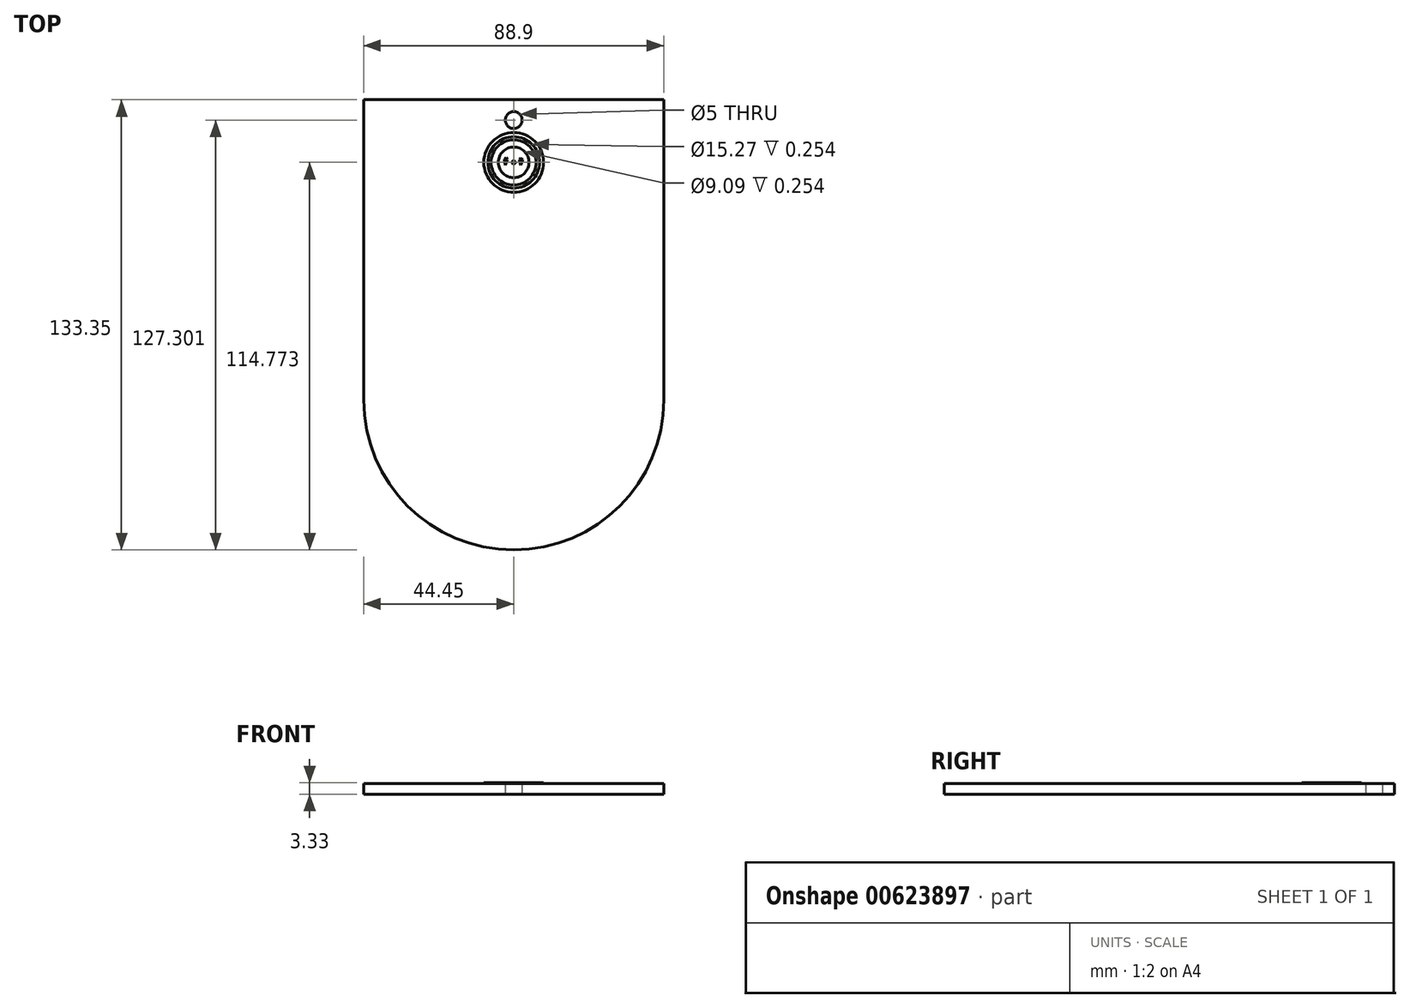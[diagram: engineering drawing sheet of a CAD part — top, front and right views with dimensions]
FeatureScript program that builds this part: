
annotation { "Feature Type Name" : "Feature", "Feature Type Description" : "" }
export const myFeature = defineFeature(function(context is Context, id is Id, definition is map)
    precondition{}
    {
        {
            var Q0;
            Q0=qCreatedBy(makeId("Top.planeOp"),FACE);
            var sketch = newSketch(context, id + "F0", { "sketchPlane" : qUnion([Q0])});
            skArc(sketch, "E0", {"start": v(-44.45, 0) * mm, "mid": v(0, -44.45) * mm, "end": v(44.45, 0) * mm});
            skLineSegment(sketch, "E1", {"start": v(-44.45, 0) * mm, "end": v(-44.45, 88.9) * mm});
            skLineSegment(sketch, "E2", {"start": v(44.45, 0) * mm, "end": v(44.45, 88.9) * mm});
            skLineSegment(sketch, "E3", {"start": v(-44.45, 88.9) * mm, "end": v(44.45, 88.9) * mm});
            skCircle(sketch, "E4", {"center": v(0, 82.85) * mm, "radius": 2.5 * mm});
            skSolve(sketch);
        }
        {
            var Q0;
            Q0=makeQuery(id+"F0.imprint","IMPRINT",FACE,{"disambiguationData":[TD([[makeQuery(id+"F0.imprint","IMPRINT",EDGE,{"derivedFrom":sQuery(id+"F0.wireOp",EDGE,"E0")}),1.0]])]});
            extrude(context, id + "F1", {"entities" : qUnion([Q0]), "depth" : 3.07 * mm, "offsetDistance" : 25.4 * mm});
        }
        {
            var Q0;
            Q0=makeQuery(id+"F1.opExtrude","CAP_FACE",FACE,{"disambiguationData":[OSD([sQuery(id+"F0.wireOp",EDGE,"E0"),sQuery(id+"F0.wireOp",EDGE,"E1"),sQuery(id+"F0.wireOp",EDGE,"E2"),sQuery(id+"F0.wireOp",EDGE,"E3"),sQuery(id+"F0.wireOp",EDGE,"E4")])],"isStart":false});
            var sketch = newSketch(context, id + "F2", { "sketchPlane" : qUnion([Q0])});
            skCircle(sketch, "E5", {"center": v(0, 70.32) * mm, "radius": 8.85 * mm});
            skCircle(sketch, "E6", {"center": v(0, 70.32) * mm, "radius": 7.63 * mm});
            skCircle(sketch, "E7", {"center": v(0, 70.32) * mm, "radius": 6.68 * mm});
            skCircle(sketch, "E8", {"center": v(0, 70.32) * mm, "radius": 4.55 * mm});
            skLineSegment(sketch, "E9", {"start": v(-2.82, 71.13) * mm, "end": v(-2.22, 71.83) * mm});
            skLineSegment(sketch, "E10", {"start": v(-2.22, 71.83) * mm, "end": v(-1.88, 71.13) * mm});
            skLineSegment(sketch, "E11", {"start": v(-1.88, 71.13) * mm, "end": v(-2.46, 69.45) * mm});
            skLineSegment(sketch, "E12", {"start": v(-2.46, 69.45) * mm, "end": v(-2.82, 71.13) * mm});
            skLineSegment(sketch, "E13", {"start": v(1.65, 71.13) * mm, "end": v(2.07, 71.62) * mm});
            skLineSegment(sketch, "E14", {"start": v(2.07, 71.62) * mm, "end": v(2.64, 71.13) * mm});
            skLineSegment(sketch, "E15", {"start": v(2.64, 71.13) * mm, "end": v(2.07, 69.54) * mm});
            skLineSegment(sketch, "E16", {"start": v(2.07, 69.54) * mm, "end": v(1.65, 71.13) * mm});
            skCircle(sketch, "E17", {"center": v(0, 70.32) * mm, "radius": 0.5 * mm});
            skSolve(sketch);
        }
        {
            var Q0;
            Q0=makeQuery(id+"F2.imprint","IMPRINT",FACE,{"disambiguationData":[TD([[makeQuery(id+"F2.imprint","IMPRINT",EDGE,{"derivedFrom":sQuery(id+"F2.wireOp",EDGE,"E7")}),1.0]])]});
            var Q1;
            Q1=makeQuery(id+"F2.imprint","IMPRINT",FACE,{"disambiguationData":[TD([[makeQuery(id+"F2.imprint","IMPRINT",EDGE,{"derivedFrom":sQuery(id+"F2.wireOp",EDGE,"E9")}),-1.0]])]});
            var Q2;
            Q2=makeQuery(id+"F2.imprint","IMPRINT",FACE,{"disambiguationData":[TD([[makeQuery(id+"F2.imprint","IMPRINT",EDGE,{"derivedFrom":sQuery(id+"F2.wireOp",EDGE,"E17")}),1.0]])]});
            var Q3;
            Q3=makeQuery(id+"F2.imprint","IMPRINT",FACE,{"disambiguationData":[TD([[makeQuery(id+"F2.imprint","IMPRINT",EDGE,{"derivedFrom":sQuery(id+"F2.wireOp",EDGE,"E13")}),-1.0]])]});
            var Q4;
            Q4=makeQuery(id+"F2.imprint","IMPRINT",FACE,{"disambiguationData":[TD([[makeQuery(id+"F2.imprint","IMPRINT",EDGE,{"derivedFrom":sQuery(id+"F2.wireOp",EDGE,"E5")}),1.0]])]});
            extrude(context, id + "F3", {"entities" : qUnion([Q0, Q1, Q2, Q3, Q4]), "operationType" : NewBodyOperationType.ADD, "depth" : 0.25 * mm, "offsetDistance" : 25.4 * mm});
        }
    });
